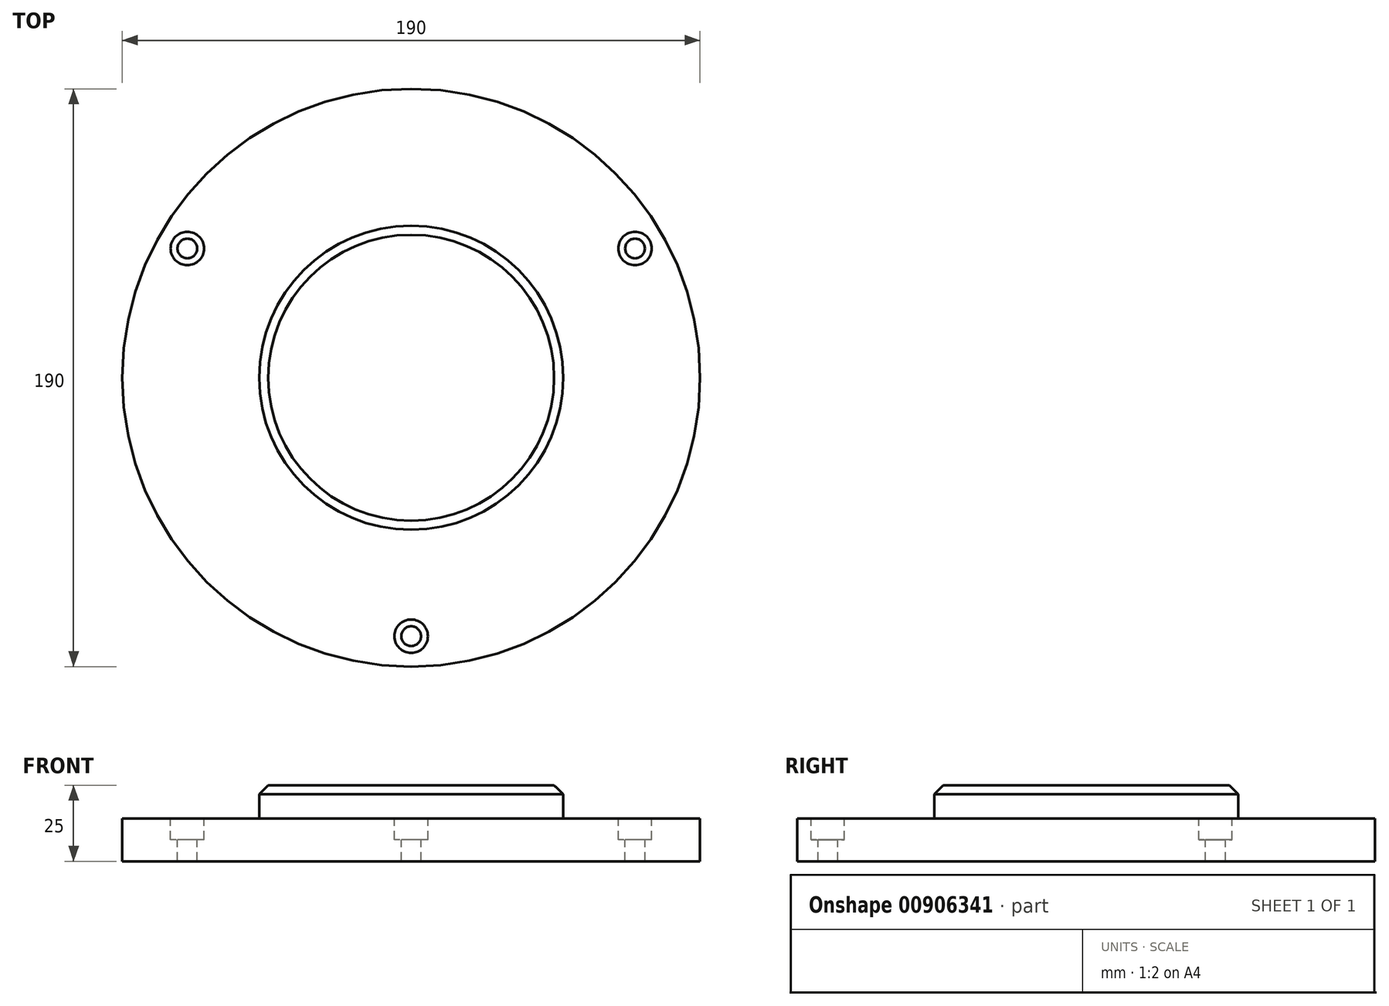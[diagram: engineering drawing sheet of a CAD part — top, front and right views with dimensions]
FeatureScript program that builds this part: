
annotation { "Feature Type Name" : "Feature", "Feature Type Description" : "" }
export const myFeature = defineFeature(function(context is Context, id is Id, definition is map)
    precondition{}
    {
        {
            var Q0;
            Q0=qCreatedBy(makeId("Top.planeOp"),FACE);
            var sketch = newSketch(context, id + "F0", { "sketchPlane" : qUnion([Q0])});
            skCircle(sketch, "E0", {"center": v(0, 0) * mm, "radius": 95 * mm});
            skSolve(sketch);
        }
        {
            var Q0;
            Q0=makeQuery(id+"F0.imprint","IMPRINT",FACE,{"disambiguationData":[TD([[makeQuery(id+"F0.imprint","IMPRINT",EDGE,{"derivedFrom":sQuery(id+"F0.wireOp",EDGE,"E0")}),1.0]])]});
            extrude(context, id + "F1", {"entities" : qUnion([Q0]), "depth" : 14 * mm, "offsetDistance" : 25 * mm});
        }
        {
            var Q0;
            Q0=makeQuery(id+"F1.opExtrude","CAP_FACE",FACE,{"disambiguationData":[OSD([sQuery(id+"F0.wireOp",EDGE,"E0")])],"isStart":false});
            var sketch = newSketch(context, id + "F2", { "sketchPlane" : qUnion([Q0])});
            skCircle(sketch, "E1", {"center": v(0, 0) * mm, "radius": 50 * mm});
            skSolve(sketch);
        }
        {
            var Q0;
            Q0=makeQuery(id+"F2.imprint","IMPRINT",FACE,{"disambiguationData":[TD([[makeQuery(id+"F2.imprint","IMPRINT",EDGE,{"derivedFrom":sQuery(id+"F2.wireOp",EDGE,"E1")}),1.0]])]});
            extrude(context, id + "F3", {"entities" : qUnion([Q0]), "operationType" : NewBodyOperationType.ADD, "depth" : 11 * mm, "offsetDistance" : 25 * mm});
        }
        {
            var Q0;
            Q0=makeQuery(id+"F3.opExtrude","CAP_EDGE",EDGE,{"disambiguationData":[OSD([sQuery(id+"F2.wireOp",EDGE,"E1")])],"isStart":false});
            chamfer(context, id + "F4", {"entities" : qUnion([Q0]), "width" : 3 * mm, "tangentPropagation" : true});
        }
        {
            var Q0;
            Q0=makeQuery(id+"F1.opExtrude","CAP_FACE",FACE,{"disambiguationData":[OSD([sQuery(id+"F0.wireOp",EDGE,"E0")])],"isStart":false});
            var sketch = newSketch(context, id + "F5", { "sketchPlane" : qUnion([Q0])});
            skLineSegment(sketch, "E2", {"start": v(0, 0) * mm, "end": v(0, -153.36) * mm, "construction": true});
            skLineSegment(sketch, "E3", {"start": v(0, 0) * mm, "end": v(-134.28, 77.53) * mm, "construction": true});
            skLineSegment(sketch, "E4", {"start": v(0, 0) * mm, "end": v(130.22, 75.18) * mm, "construction": true});
            skCircle(sketch, "E5", {"center": v(0, 0) * mm, "radius": 85 * mm, "construction": true});
            skCircle(sketch, "E6", {"center": v(0, -85) * mm, "radius": 5.5 * mm});
            skCircle(sketch, "E7", {"center": v(-73.61, 42.5) * mm, "radius": 5.5 * mm});
            skCircle(sketch, "E8", {"center": v(73.61, 42.5) * mm, "radius": 5.5 * mm});
            skSolve(sketch);
        }
        {
            var Q0;
            Q0 = qSketchRegion(id + "F5", true);
            extrude(context, id + "F6", {"entities" : qUnion([Q0]), "operationType" : NewBodyOperationType.REMOVE, "oppositeDirection" : true, "depth" : 7 * mm, "offsetDistance" : 25 * mm});
        }
        {
            var Q0;
            Q0=makeQuery(id+"F6.boolean.opBoolean","COPY",FACE,{"derivedFrom":makeQuery(id+"F6.opExtrude","CAP_FACE",FACE,{"disambiguationData":[OSD([sQuery(id+"F5.wireOp",EDGE,"E6")])],"isStart":false})});
            var sketch = newSketch(context, id + "F7", { "sketchPlane" : qUnion([Q0])});
            skCircle(sketch, "E9", {"center": v(0, -85) * mm, "radius": 3.25 * mm});
            skCircle(sketch, "E10", {"center": v(73.61, 42.5) * mm, "radius": 3.25 * mm});
            skCircle(sketch, "E11", {"center": v(-73.61, 42.5) * mm, "radius": 3.25 * mm});
            skSolve(sketch);
        }
        {
            var Q0;
            Q0 = qSketchRegion(id + "F7", true);
            extrude(context, id + "F8", {"entities" : qUnion([Q0]), "operationType" : NewBodyOperationType.REMOVE, "oppositeDirection" : true, "depth" : 25 * mm, "offsetDistance" : 25 * mm});
        }
    });
